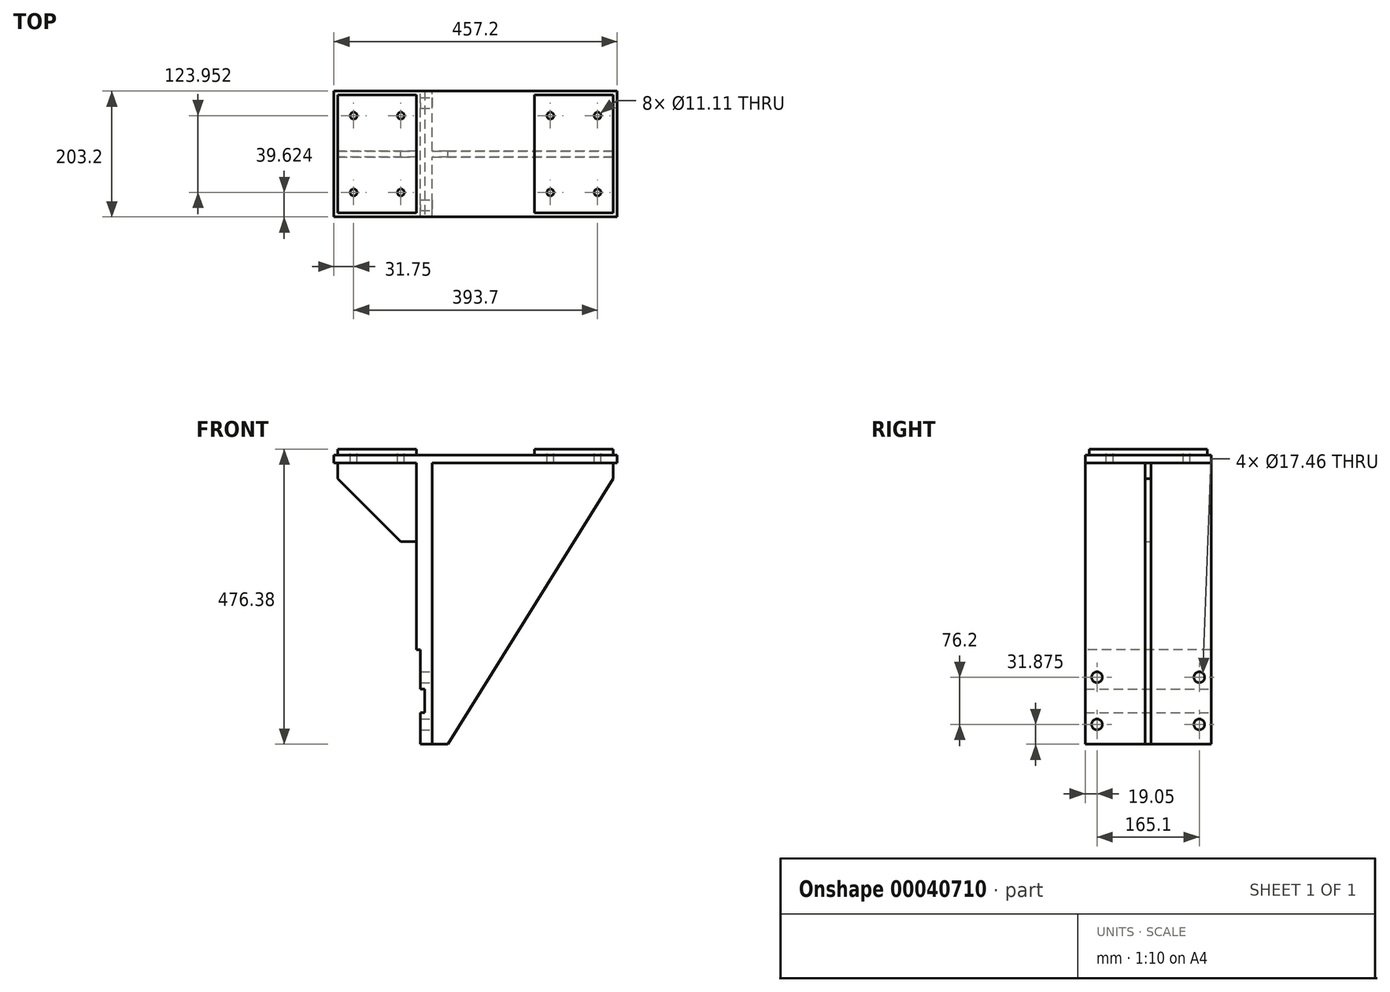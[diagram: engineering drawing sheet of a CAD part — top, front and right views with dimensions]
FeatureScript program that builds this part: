
annotation { "Feature Type Name" : "Feature", "Feature Type Description" : "" }
export const myFeature = defineFeature(function(context is Context, id is Id, definition is map)
    precondition{}
    {
        {
            var Q0;
            Q0=qCreatedBy(makeId("Top.planeOp"),FACE);
            var sketch = newSketch(context, id + "F0", { "sketchPlane" : qUnion([Q0])});
            skLineSegment(sketch, "E0.rect.bottom", {"start": v(-228.6, 101.6) * mm, "end": v(228.6, 101.6) * mm});
            skLineSegment(sketch, "E0.rect.top", {"start": v(-228.6, -101.6) * mm, "end": v(228.6, -101.6) * mm});
            skLineSegment(sketch, "E0.rect.left", {"start": v(-228.6, 101.6) * mm, "end": v(-228.6, -101.6) * mm});
            skLineSegment(sketch, "E0.rect.right", {"start": v(228.6, 101.6) * mm, "end": v(228.6, -101.6) * mm});
            skPoint(sketch, "E0.rect.middle", {"position": v(0, 0) * mm});
            skSolve(sketch);
        }
        {
            var Q0;
            Q0 = qSketchRegion(id + "F0", true);
            extrude(context, id + "F1", {"entities" : qUnion([Q0]), "depth" : 12.7 * mm});
        }
        {
            var Q0;
            Q0=makeQuery(id+"F1.opExtrude","CAP_FACE",FACE,{"disambiguationData":[OSD([sQuery(id+"F0.wireOp",EDGE,"E0.rect.bottom"),sQuery(id+"F0.wireOp",EDGE,"E0.rect.top"),sQuery(id+"F0.wireOp",EDGE,"E0.rect.left"),sQuery(id+"F0.wireOp",EDGE,"E0.rect.right")])],"isStart":false});
            var sketch = newSketch(context, id + "F2", { "sketchPlane" : qUnion([Q0])});
            skLineSegment(sketch, "E1.0", {"start": v(222.25, 95.25) * mm, "end": v(95.25, 95.25) * mm});
            skLineSegment(sketch, "E1.1", {"start": v(222.25, -95.25) * mm, "end": v(222.25, 95.25) * mm});
            skLineSegment(sketch, "E1.2", {"start": v(-222.25, -95.25) * mm, "end": v(-95.25, -95.25) * mm});
            skLineSegment(sketch, "E1.3", {"start": v(-222.25, 95.25) * mm, "end": v(-222.25, -95.25) * mm});
            skLineSegment(sketch, "E2.0", {"start": v(-95.25, 95.25) * mm, "end": v(-95.25, -95.25) * mm});
            skLineSegment(sketch, "E3.0", {"start": v(95.25, -95.25) * mm, "end": v(95.25, 95.25) * mm});
            skLineSegment(sketch, "E4.trimOffspring", {"start": v(-95.25, 95.25) * mm, "end": v(-222.25, 95.25) * mm});
            skLineSegment(sketch, "E5.trimOffspring", {"start": v(95.25, -95.25) * mm, "end": v(222.25, -95.25) * mm});
            skSolve(sketch);
        }
        {
            var Q0;
            Q0 = qSketchRegion(id + "F2", true);
            extrude(context, id + "F3", {"entities" : qUnion([Q0]), "operationType" : NewBodyOperationType.ADD, "depth" : 9.52 * mm});
        }
        {
            var Q0;
            Q0=makeQuery(id+"F3.opExtrude","CAP_FACE",FACE,{"disambiguationData":[OSD([sQuery(id+"F2.wireOp",EDGE,"E1.2"),sQuery(id+"F2.wireOp",EDGE,"E1.3"),sQuery(id+"F2.wireOp",EDGE,"E2.0"),sQuery(id+"F2.wireOp",EDGE,"E4.trimOffspring")])],"isStart":false});
            var sketch = newSketch(context, id + "F4", { "sketchPlane" : qUnion([Q0])});
            skLineSegment(sketch, "E6", {"start": v(-222.25, 0) * mm, "end": v(222.2, 0) * mm, "construction": true});
            skLineSegment(sketch, "E7.0", {"start": v(222.25, 95.25) * mm, "end": v(95.25, 95.25) * mm, "construction": true});
            skLineSegment(sketch, "E8.0", {"start": v(95.25, -95.25) * mm, "end": v(222.25, -95.25) * mm, "construction": true});
            skLineSegment(sketch, "E9", {"start": v(-158.75, 95.25) * mm, "end": v(-158.75, -95.25) * mm, "construction": true});
            skLineSegment(sketch, "E10", {"start": v(158.75, 95.25) * mm, "end": v(158.75, -95.25) * mm, "construction": true});
            skLineSegment(sketch, "E11.0", {"start": v(-196.85, 95.25) * mm, "end": v(-196.85, -95.25) * mm, "construction": true});
            skLineSegment(sketch, "E12.0", {"start": v(-120.65, 95.25) * mm, "end": v(-120.65, -95.25) * mm, "construction": true});
            skLineSegment(sketch, "E13.0", {"start": v(120.65, 95.25) * mm, "end": v(120.65, -95.25) * mm, "construction": true});
            skLineSegment(sketch, "E14.0", {"start": v(-222.25, 61.98) * mm, "end": v(222.2, 61.98) * mm, "construction": true});
            skPoint(sketch, "E15", {"position": v(-196.85, 61.98) * mm});
            skPoint(sketch, "E16", {"position": v(-120.65, 61.98) * mm});
            skPoint(sketch, "E17", {"position": v(120.65, 61.98) * mm});
            skPoint(sketch, "E18.MirrorP", {"position": v(196.85, 61.98) * mm});
            skPoint(sketch, "E19.MirrorP", {"position": v(-196.85, -61.98) * mm});
            skPoint(sketch, "E20.MirrorP", {"position": v(-120.65, -61.98) * mm});
            skPoint(sketch, "E21.MirrorP", {"position": v(120.65, -61.98) * mm});
            skPoint(sketch, "E22.MirrorP", {"position": v(196.85, -61.98) * mm});
            skSolve(sketch);
        }
        {
            var Q0;
            Q0=sQuery(id+"F4.wireOp",VERTEX,"E15");
            var Q1;
            Q1=sQuery(id+"F4.wireOp",VERTEX,"E16");
            var Q2;
            Q2=sQuery(id+"F4.wireOp",VERTEX,"E19.MirrorP");
            var Q3;
            Q3=sQuery(id+"F4.wireOp",VERTEX,"E20.MirrorP");
            var Q4;
            Q4=sQuery(id+"F4.wireOp",VERTEX,"E17");
            var Q5;
            Q5=sQuery(id+"F4.wireOp",VERTEX,"E18.MirrorP");
            var Q6;
            Q6=sQuery(id+"F4.wireOp",VERTEX,"E22.MirrorP");
            var Q7;
            Q7=sQuery(id+"F4.wireOp",VERTEX,"E21.MirrorP");
            var Q8;
            Q8=makeQuery(id+"F1.opExtrude","SWEPT_BODY",BODY,{"disambiguationData":[OSD([sQuery(id+"F0.wireOp",EDGE,"E0.rect.bottom"),sQuery(id+"F0.wireOp",EDGE,"E0.rect.top"),sQuery(id+"F0.wireOp",EDGE,"E0.rect.left"),sQuery(id+"F0.wireOp",EDGE,"E0.rect.right")])]});
            hole(context, id + "F5", {"style" : HoleStyle.SIMPLE, "holeDiameter" : 11.1 * mm, "endStyle" : HoleEndStyle.THROUGH, "locations" : qUnion([Q0, Q1, Q2, Q3, Q4, Q5, Q6, Q7]), "scope" : qUnion([Q8])});
        }
        {
            var Q0;
            Q0=qCreatedBy(makeId("Front.planeOp"),FACE);
            var sketch = newSketch(context, id + "F6", { "sketchPlane" : qUnion([Q0])});
            skLineSegment(sketch, "E23.0", {"start": v(-228.6, 0) * mm, "end": v(228.6, 0) * mm, "construction": true});
            skLineSegment(sketch, "E24.0", {"start": v(-228.6, 12.7) * mm, "end": v(-228.6, 0) * mm, "construction": true});
            skLineSegment(sketch, "E25.0", {"start": v(-222.25, 12.7) * mm, "end": v(-222.25, 0) * mm, "construction": true});
            skLineSegment(sketch, "E26", {"start": v(-222.25, 0) * mm, "end": v(-222.25, -25.4) * mm});
            skLineSegment(sketch, "E27", {"start": v(-222.25, -25.4) * mm, "end": v(-120.65, -127) * mm});
            skLineSegment(sketch, "E28", {"start": v(-120.65, -127) * mm, "end": v(-95.25, -127) * mm});
            skLineSegment(sketch, "E29", {"start": v(-95.25, -127) * mm, "end": v(-95.25, 0) * mm});
            skLineSegment(sketch, "E30", {"start": v(-95.25, 0) * mm, "end": v(-222.25, 0) * mm});
            skSolve(sketch);
        }
        {
            var Q0;
            Q0 = qSketchRegion(id + "F6", true);
            extrude(context, id + "F7", {"entities" : qUnion([Q0]), "operationType" : NewBodyOperationType.ADD, "endBound" : BoundingType.SYMMETRIC, "depth" : 9.52 * mm});
        }
        {
            var Q0;
            Q0=qCreatedBy(makeId("Front.planeOp"),FACE);
            var sketch = newSketch(context, id + "F8", { "sketchPlane" : qUnion([Q0])});
            skLineSegment(sketch, "E31.0", {"start": v(228.6, 12.7) * mm, "end": v(228.6, 0) * mm, "construction": true});
            skLineSegment(sketch, "E32.0", {"start": v(222.25, 12.7) * mm, "end": v(222.25, 0) * mm, "construction": true});
            skLineSegment(sketch, "E33", {"start": v(222.25, 0) * mm, "end": v(222.25, -25.4) * mm});
            skLineSegment(sketch, "E34", {"start": v(222.25, -25.4) * mm, "end": v(-44.45, -454.15) * mm});
            skLineSegment(sketch, "E35", {"start": v(-44.45, -454.15) * mm, "end": v(-69.85, -454.15) * mm});
            skLineSegment(sketch, "E36", {"start": v(-69.85, -454.15) * mm, "end": v(-69.85, 0) * mm});
            skLineSegment(sketch, "E37", {"start": v(-69.85, 0) * mm, "end": v(222.25, 0) * mm});
            skSolve(sketch);
        }
        {
            var Q0;
            Q0 = qSketchRegion(id + "F8", true);
            extrude(context, id + "F9", {"entities" : qUnion([Q0]), "operationType" : NewBodyOperationType.ADD, "endBound" : BoundingType.SYMMETRIC, "depth" : 9.52 * mm});
        }
        {
            var Q0;
            Q0=qCreatedBy(makeId("Front.planeOp"),FACE);
            var sketch = newSketch(context, id + "F10", { "sketchPlane" : qUnion([Q0])});
            skLineSegment(sketch, "E38.0", {"start": v(-95.25, -127) * mm, "end": v(-95.25, 0) * mm, "construction": true});
            skLineSegment(sketch, "E39.0", {"start": v(-69.85, -454.15) * mm, "end": v(-69.85, 0) * mm, "construction": true});
            skLineSegment(sketch, "E40.bottom", {"start": v(-95.25, 0) * mm, "end": v(-69.85, 0) * mm});
            skLineSegment(sketch, "E40.top", {"start": v(-95.25, -454.15) * mm, "end": v(-69.85, -454.15) * mm});
            skLineSegment(sketch, "E40.left", {"start": v(-95.25, 0) * mm, "end": v(-95.25, -454.15) * mm});
            skLineSegment(sketch, "E40.right", {"start": v(-69.85, 0) * mm, "end": v(-69.85, -454.15) * mm});
            skSolve(sketch);
        }
        {
            var Q0;
            Q0 = qSketchRegion(id + "F10", true);
            extrude(context, id + "F11", {"entities" : qUnion([Q0]), "operationType" : NewBodyOperationType.ADD, "endBound" : BoundingType.SYMMETRIC, "depth" : 203.2 * mm});
        }
        {
            var Q0;
            Q0=makeQuery(id+"F11.boolean.opBoolean","MERGE",FACE,{"derivedFrom":[makeQuery(id+"F1.opExtrude","SWEPT_FACE",FACE,{"disambiguationData":[OSD([sQuery(id+"F0.wireOp",EDGE,"E0.rect.top")])]}),makeQuery(id+"F11.opExtrude","CAP_FACE",FACE,{"disambiguationData":[OSD([sQuery(id+"F10.wireOp",EDGE,"E40.bottom"),sQuery(id+"F10.wireOp",EDGE,"E40.top"),sQuery(id+"F10.wireOp",EDGE,"E40.left"),sQuery(id+"F10.wireOp",EDGE,"E40.right")])],"isStart":false})]});
            var sketch = newSketch(context, id + "F12", { "sketchPlane" : qUnion([Q0])});
            skLineSegment(sketch, "E41.0", {"start": v(-95.25, -454.15) * mm, "end": v(-69.85, -454.15) * mm, "construction": true});
            skLineSegment(sketch, "E42.0", {"start": v(-95.25, 0) * mm, "end": v(-95.25, -454.15) * mm, "construction": true});
            skLineSegment(sketch, "E43.0", {"start": v(-95.25, -301.75) * mm, "end": v(-69.85, -301.75) * mm, "construction": true});
            skLineSegment(sketch, "E44.0", {"start": v(-88.9, 0) * mm, "end": v(-88.9, -454.15) * mm, "construction": true});
            skLineSegment(sketch, "E45.bottom", {"start": v(-88.9, -301.75) * mm, "end": v(-133.45, -301.75) * mm});
            skLineSegment(sketch, "E45.top", {"start": v(-88.9, -461.11) * mm, "end": v(-133.45, -461.11) * mm});
            skLineSegment(sketch, "E45.left", {"start": v(-88.9, -301.75) * mm, "end": v(-88.9, -461.11) * mm});
            skLineSegment(sketch, "E45.right", {"start": v(-133.45, -301.75) * mm, "end": v(-133.45, -461.11) * mm});
            skSolve(sketch);
        }
        {
            var Q0;
            Q0 = qSketchRegion(id + "F12", true);
            extrude(context, id + "F13", {"entities" : qUnion([Q0]), "operationType" : NewBodyOperationType.REMOVE, "endBound" : BoundingType.THROUGH_ALL, "oppositeDirection" : true, "depth" : 25.4 * mm});
        }
        {
            var Q0;
            Q0=makeQuery(id+"F11.boolean.opBoolean","MERGE",FACE,{"derivedFrom":[makeQuery(id+"F1.opExtrude","SWEPT_FACE",FACE,{"disambiguationData":[OSD([sQuery(id+"F0.wireOp",EDGE,"E0.rect.top")])]}),makeQuery(id+"F11.opExtrude","CAP_FACE",FACE,{"disambiguationData":[OSD([sQuery(id+"F10.wireOp",EDGE,"E40.bottom"),sQuery(id+"F10.wireOp",EDGE,"E40.top"),sQuery(id+"F10.wireOp",EDGE,"E40.left"),sQuery(id+"F10.wireOp",EDGE,"E40.right")])],"isStart":false})]});
            var sketch = newSketch(context, id + "F14", { "sketchPlane" : qUnion([Q0])});
            skLineSegment(sketch, "E46.0", {"start": v(-222.25, 22.23) * mm, "end": v(-95.25, 22.23) * mm, "construction": true});
            skLineSegment(sketch, "E47.0", {"start": v(-222.25, -384.18) * mm, "end": v(-95.25, -384.18) * mm, "construction": true});
            skLineSegment(sketch, "E48.0", {"start": v(-222.25, -365.13) * mm, "end": v(-82.04, -365.13) * mm, "construction": true});
            skLineSegment(sketch, "E49.0", {"start": v(-88.9, -301.75) * mm, "end": v(-88.9, -454.15) * mm, "construction": true});
            skLineSegment(sketch, "E50.0", {"start": v(-82.04, -301.75) * mm, "end": v(-82.04, -454.15) * mm});
            skLineSegment(sketch, "E51.MirrorCS", {"start": v(-222.25, -403.23) * mm, "end": v(-82.04, -403.23) * mm, "construction": true});
            skPoint(sketch, "E52.orphan", {"position": v(-95.25, -365.13) * mm});
            skPoint(sketch, "E53.orphan", {"position": v(-95.25, -403.23) * mm});
            skLineSegment(sketch, "E54.bottom", {"start": v(-82.04, -365.13) * mm, "end": v(-178.88, -365.13) * mm});
            skLineSegment(sketch, "E54.top", {"start": v(-82.04, -403.23) * mm, "end": v(-178.88, -403.23) * mm});
            skLineSegment(sketch, "E54.left", {"start": v(-82.04, -365.13) * mm, "end": v(-82.04, -403.23) * mm});
            skLineSegment(sketch, "E54.right", {"start": v(-178.88, -365.13) * mm, "end": v(-178.88, -403.23) * mm});
            skSolve(sketch);
        }
        {
            var Q0;
            Q0 = qSketchRegion(id + "F14", true);
            extrude(context, id + "F15", {"entities" : qUnion([Q0]), "operationType" : NewBodyOperationType.REMOVE, "endBound" : BoundingType.THROUGH_ALL, "oppositeDirection" : true, "depth" : 25.4 * mm});
        }
        {
            var Q0;
            {var subQ0=sQuery(id+"F10.wireOp",EDGE,"E40.right");var subQ2=sQuery(id+"F0.wireOp",EDGE,"E0.rect.top");Q0=makeQuery(id+"F11.boolean.opBoolean","SPLIT",FACE,{"disambiguationData":[TD([makeQuery(id+"F1.opExtrude","SWEPT_FACE",FACE,{"disambiguationData":[OSD([subQ2])]})])],"derivedFrom":makeQuery(id+"F11.opExtrude","SWEPT_FACE",FACE,{"disambiguationData":[OSD([subQ0])]})});}
            var sketch = newSketch(context, id + "F16", { "sketchPlane" : qUnion([Q0])});
            skLineSegment(sketch, "E55.0", {"start": v(101.6, -365.13) * mm, "end": v(-101.6, -365.13) * mm, "construction": true});
            skLineSegment(sketch, "E56.0", {"start": v(101.6, -403.23) * mm, "end": v(-101.6, -403.23) * mm, "construction": true});
            skLineSegment(sketch, "E57", {"start": v(-101.6, -365.13) * mm, "end": v(-101.6, -403.23) * mm, "construction": true});
            skLineSegment(sketch, "E58", {"start": v(-101.6, -384.18) * mm, "end": v(113.68, -384.18) * mm, "construction": true});
            skLineSegment(sketch, "E59.0", {"start": v(-101.6, -454.15) * mm, "end": v(101.6, -454.15) * mm, "construction": true});
            skLineSegment(sketch, "E60", {"start": v(0, -454.15) * mm, "end": v(0, -282.9) * mm, "construction": true});
            skLineSegment(sketch, "E61.0", {"start": v(-101.6, -346.08) * mm, "end": v(113.68, -346.08) * mm, "construction": true});
            skLineSegment(sketch, "E62.MirrorCS", {"start": v(-101.6, -422.28) * mm, "end": v(113.68, -422.28) * mm, "construction": true});
            skLineSegment(sketch, "E63.0", {"start": v(-82.55, -454.15) * mm, "end": v(-82.55, -282.9) * mm, "construction": true});
            skPoint(sketch, "E64", {"position": v(-82.55, -346.08) * mm});
            skPoint(sketch, "E65", {"position": v(-82.55, -422.28) * mm});
            skPoint(sketch, "E66.MirrorP", {"position": v(82.55, -422.28) * mm});
            skPoint(sketch, "E67.MirrorP", {"position": v(82.55, -346.08) * mm});
            skSolve(sketch);
        }
        {
            var Q0;
            Q0=sQuery(id+"F16.wireOp",VERTEX,"E64");
            var Q1;
            Q1=sQuery(id+"F16.wireOp",VERTEX,"E65");
            var Q2;
            Q2=sQuery(id+"F16.wireOp",VERTEX,"E66.MirrorP");
            var Q3;
            Q3=sQuery(id+"F16.wireOp",VERTEX,"E67.MirrorP");
            var Q4;
            Q4=makeQuery(id+"F1.opExtrude","SWEPT_BODY",BODY,{"disambiguationData":[OSD([sQuery(id+"F0.wireOp",EDGE,"E0.rect.bottom"),sQuery(id+"F0.wireOp",EDGE,"E0.rect.top"),sQuery(id+"F0.wireOp",EDGE,"E0.rect.left"),sQuery(id+"F0.wireOp",EDGE,"E0.rect.right")])]});
            hole(context, id + "F17", {"style" : HoleStyle.SIMPLE, "holeDiameter" : 17.46 * mm, "endStyle" : HoleEndStyle.THROUGH, "locations" : qUnion([Q0, Q1, Q2, Q3]), "scope" : qUnion([Q4])});
        }
    });
